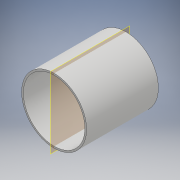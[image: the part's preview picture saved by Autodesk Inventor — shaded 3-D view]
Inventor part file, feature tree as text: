
AUTODESK INVENTOR PART (.ipt)
format: ipt  version: 2017 (Build 210142000, 142)  size: 100,352 bytes
history: native  units: mm
features: extrude x1, sketch x1
ambient origin geometry x8: Origin, YZ Plane, XZ Plane, XY Plane, X Axis, Y Axis, Z Axis, Center Point
bodies: Solid1 (feature_tree)
feature tree (2):
  extrude  "Extrusion1"  Depth=84.0mm
  sketch  "Sketch1"  dims[d0=76.0mm d1=2.0mm d2=84.0mm d3=0.0mm]
